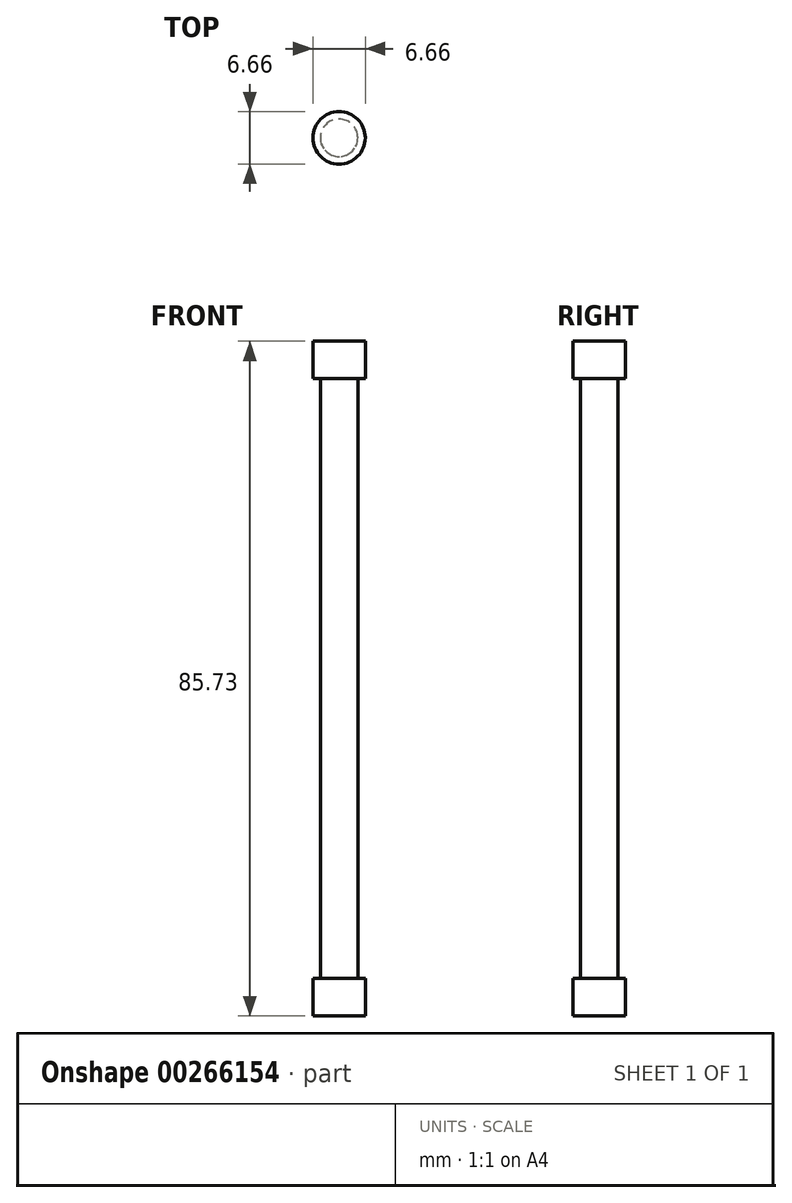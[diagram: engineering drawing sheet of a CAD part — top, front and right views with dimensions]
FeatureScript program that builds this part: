
annotation { "Feature Type Name" : "Feature", "Feature Type Description" : "" }
export const myFeature = defineFeature(function(context is Context, id is Id, definition is map)
    precondition{}
    {
        {
            var Q0;
            Q0=qCreatedBy(makeId("Top.planeOp"),FACE);
            var sketch = newSketch(context, id + "F0", { "sketchPlane" : qUnion([Q0])});
            skCircle(sketch, "E0", {"center": v(0, 0) * mm, "radius": 2.38 * mm});
            skSolve(sketch);
        }
        {
            var Q0;
            Q0=makeQuery(id+"F0.imprint","IMPRINT",FACE,{"disambiguationData":[TD([[makeQuery(id+"F0.imprint","IMPRINT",EDGE,{"derivedFrom":sQuery(id+"F0.wireOp",EDGE,"E0")}),1.0]])]});
            extrude(context, id + "F1", {"entities" : qUnion([Q0]), "depth" : 85.72 * mm});
        }
        {
            var Q0;
            Q0=makeQuery(id+"F1.opExtrude","CAP_FACE",FACE,{"disambiguationData":[OSD([sQuery(id+"F0.wireOp",EDGE,"E0")])],"isStart":true});
            var sketch = newSketch(context, id + "F2", { "sketchPlane" : qUnion([Q0])});
            skCircle(sketch, "E1", {"center": v(0, 0) * mm, "radius": 3.33 * mm});
            skSolve(sketch);
        }
        {
            var Q0;
            Q0=makeQuery(id+"F2.imprint","IMPRINT",FACE,{"disambiguationData":[TD([[makeQuery(id+"F2.imprint","IMPRINT",EDGE,{"derivedFrom":sQuery(id+"F2.wireOp",EDGE,"E1")}),1.0]])]});
            extrude(context, id + "F3", {"entities" : qUnion([Q0]), "operationType" : NewBodyOperationType.ADD, "oppositeDirection" : true, "depth" : 4.76 * mm});
        }
        {
            var Q0;
            Q0=makeQuery(id+"F1.opExtrude","CAP_FACE",FACE,{"disambiguationData":[OSD([sQuery(id+"F0.wireOp",EDGE,"E0")])],"isStart":false});
            var sketch = newSketch(context, id + "F4", { "sketchPlane" : qUnion([Q0])});
            skCircle(sketch, "E2", {"center": v(0, 0) * mm, "radius": 3.33 * mm});
            skSolve(sketch);
        }
        {
            var Q0;
            Q0=makeQuery(id+"F4.imprint","IMPRINT",FACE,{"disambiguationData":[TD([[makeQuery(id+"F4.imprint","IMPRINT",EDGE,{"derivedFrom":sQuery(id+"F4.wireOp",EDGE,"E2")}),1.0]])]});
            extrude(context, id + "F5", {"entities" : qUnion([Q0]), "operationType" : NewBodyOperationType.ADD, "oppositeDirection" : true, "depth" : 4.76 * mm});
        }
    });
